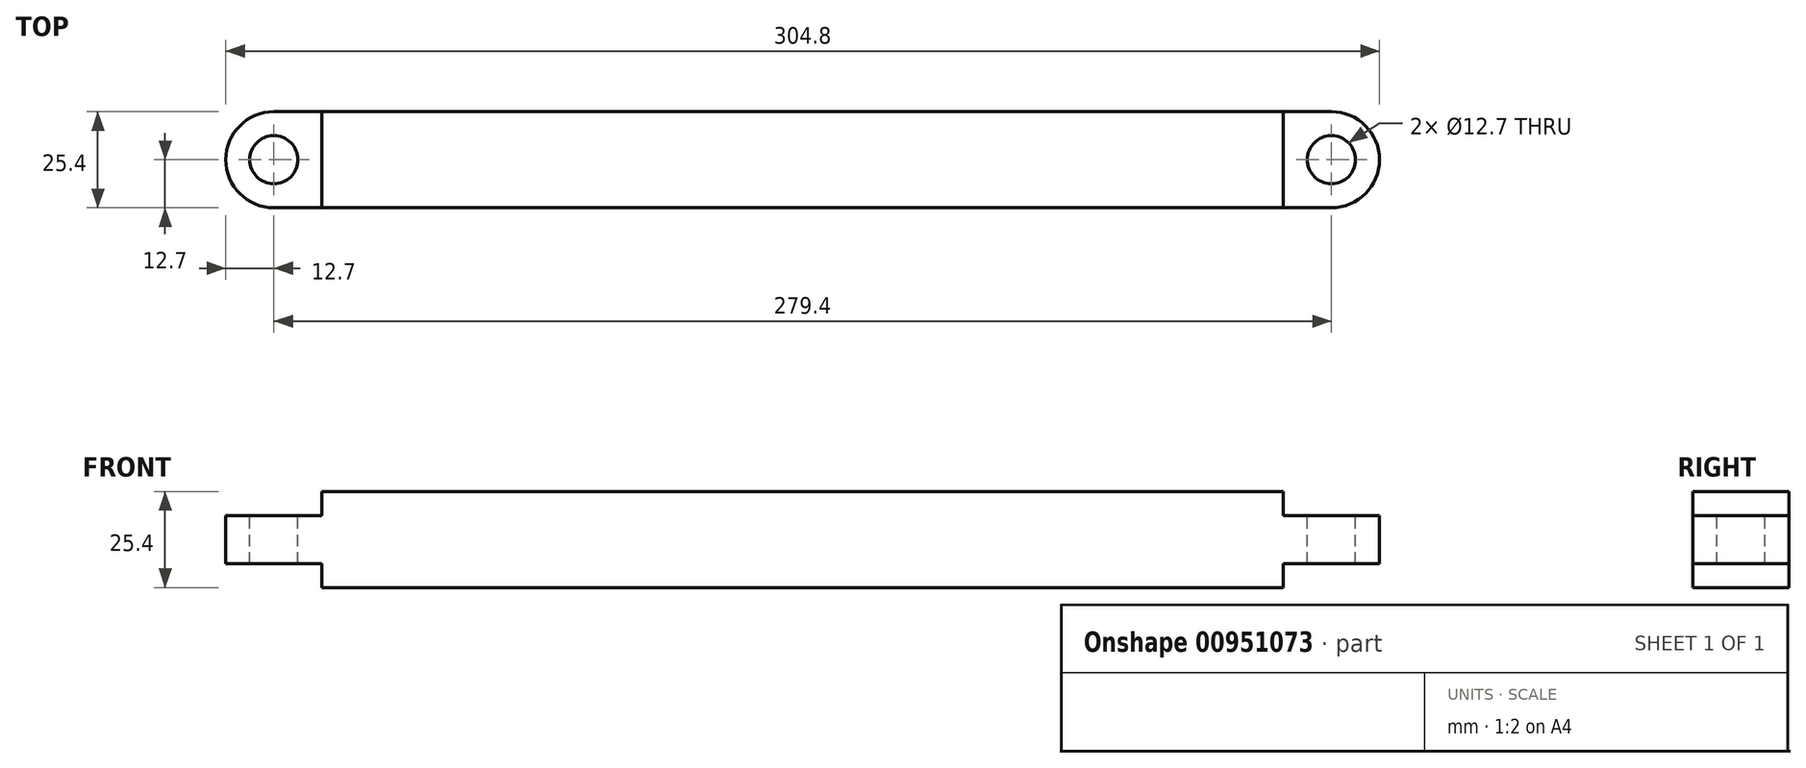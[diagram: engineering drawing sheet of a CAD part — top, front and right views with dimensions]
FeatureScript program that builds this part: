
annotation { "Feature Type Name" : "Feature", "Feature Type Description" : "" }
export const myFeature = defineFeature(function(context is Context, id is Id, definition is map)
    precondition{}
    {
        {
            var Q0;
            Q0=qCreatedBy(makeId("Top.planeOp"),FACE);
            var sketch = newSketch(context, id + "F0", { "sketchPlane" : qUnion([Q0])});
            skLineSegment(sketch, "E0.bottom", {"start": v(139.7, -12.7) * mm, "end": v(-139.7, -12.7) * mm});
            skLineSegment(sketch, "E0.top", {"start": v(139.7, 12.7) * mm, "end": v(-139.7, 12.7) * mm});
            skLineSegment(sketch, "E0.left", {"start": v(139.7, -12.7) * mm, "end": v(139.7, 12.7) * mm});
            skLineSegment(sketch, "E0.right", {"start": v(-139.7, -12.7) * mm, "end": v(-139.7, 12.7) * mm});
            skPoint(sketch, "E0.middle", {"position": v(0, 0) * mm});
            skArc(sketch, "E1", {"start": v(139.7, 12.7) * mm, "mid": v(152.4, 0) * mm, "end": v(139.7, -12.7) * mm});
            skArc(sketch, "E2", {"start": v(-139.7, 12.7) * mm, "mid": v(-152.4, 0) * mm, "end": v(-139.7, -12.7) * mm});
            skSolve(sketch);
        }
        {
            var Q0;
            Q0 = qSketchRegion(id + "F0", true);
            extrude(context, id + "F1", {"entities" : qUnion([Q0]), "depth" : 25.4 * mm, "offsetDistance" : 25.4 * mm});
        }
        {
            var Q0;
            Q0=makeQuery(id+"F1.opExtrude","CAP_FACE",FACE,{"disambiguationData":[OSD([sQuery(id+"F0.wireOp",EDGE,"E0.bottom"),sQuery(id+"F0.wireOp",EDGE,"E0.top"),sQuery(id+"F0.wireOp",EDGE,"E1"),sQuery(id+"F0.wireOp",EDGE,"E2")])],"isStart":false});
            var sketch = newSketch(context, id + "F2", { "sketchPlane" : qUnion([Q0])});
            skCircle(sketch, "E3", {"center": v(-139.7, 0) * mm, "radius": 6.35 * mm});
            skCircle(sketch, "E4", {"center": v(139.7, 0) * mm, "radius": 6.35 * mm});
            skSolve(sketch);
        }
        {
            var Q0;
            Q0 = qSketchRegion(id + "F2", true);
            var Q1;
            Q1=makeQuery(id+"F1.opExtrude","CAP_FACE",FACE,{"disambiguationData":[OSD([sQuery(id+"F0.wireOp",EDGE,"E0.bottom"),sQuery(id+"F0.wireOp",EDGE,"E0.top"),sQuery(id+"F0.wireOp",EDGE,"E1"),sQuery(id+"F0.wireOp",EDGE,"E2")])],"isStart":true});
            extrude(context, id + "F3", {"entities" : qUnion([Q0]), "operationType" : NewBodyOperationType.REMOVE, "endBound" : BoundingType.UP_TO_SURFACE, "oppositeDirection" : true, "depth" : 25.4 * mm, "endBoundEntityFace" : qUnion([Q1]), "offsetDistance" : 25.4 * mm});
        }
        {
            var Q0;
            Q0=makeQuery(id+"F1.opExtrude","SWEPT_FACE",FACE,{"disambiguationData":[OSD([sQuery(id+"F0.wireOp",EDGE,"E0.bottom")])]});
            var sketch = newSketch(context, id + "F4", { "sketchPlane" : qUnion([Q0])});
            skLineSegment(sketch, "E5.bottom", {"start": v(-96.3, 19.05) * mm, "end": v(-127, 19.05) * mm, "construction": true});
            skLineSegment(sketch, "E5.top", {"start": v(-96.3, 6.35) * mm, "end": v(-127, 6.35) * mm, "construction": true});
            skLineSegment(sketch, "E5.left", {"start": v(-127, 19.05) * mm, "end": v(-127, 6.35) * mm, "construction": true});
            skLineSegment(sketch, "E5.right", {"start": v(-96.3, 19.05) * mm, "end": v(-96.3, 6.35) * mm, "construction": true});
            skLineSegment(sketch, "E6", {"start": v(-127, 19.05) * mm, "end": v(-127, 25.4) * mm});
            skLineSegment(sketch, "E7", {"start": v(-127, 25.4) * mm, "end": v(-279.4, 25.4) * mm});
            skLineSegment(sketch, "E8", {"start": v(-279.4, 25.4) * mm, "end": v(-279.4, 19.05) * mm});
            skLineSegment(sketch, "E9", {"start": v(-279.4, 19.05) * mm, "end": v(-127, 19.05) * mm});
            skLineSegment(sketch, "E10", {"start": v(-127, 6.35) * mm, "end": v(-127, 0) * mm});
            skLineSegment(sketch, "E11", {"start": v(-127, 0) * mm, "end": v(-279.4, 0) * mm});
            skLineSegment(sketch, "E12", {"start": v(-279.4, 0) * mm, "end": v(-279.4, 6.35) * mm});
            skLineSegment(sketch, "E13", {"start": v(-279.4, 6.35) * mm, "end": v(-127, 6.35) * mm});
            skLineSegment(sketch, "E14", {"start": v(127, 25.4) * mm, "end": v(279.4, 25.4) * mm});
            skLineSegment(sketch, "E15", {"start": v(127, 19.05) * mm, "end": v(279.4, 19.05) * mm});
            skLineSegment(sketch, "E16", {"start": v(127, 6.35) * mm, "end": v(279.4, 6.35) * mm});
            skLineSegment(sketch, "E17", {"start": v(127, 0) * mm, "end": v(279.4, 0) * mm});
            skLineSegment(sketch, "E18", {"start": v(127, 25.4) * mm, "end": v(127, 19.05) * mm});
            skLineSegment(sketch, "E19", {"start": v(127, 6.35) * mm, "end": v(127, 0) * mm});
            skLineSegment(sketch, "E20", {"start": v(279.4, 25.4) * mm, "end": v(279.4, 19.05) * mm});
            skLineSegment(sketch, "E21", {"start": v(279.4, 6.35) * mm, "end": v(279.4, 0) * mm});
            skSolve(sketch);
        }
        {
            var Q0;
            Q0 = qSketchRegion(id + "F4", true);
            extrude(context, id + "F5", {"entities" : qUnion([Q0]), "operationType" : NewBodyOperationType.REMOVE, "endBound" : BoundingType.THROUGH_ALL, "oppositeDirection" : true, "depth" : 25.4 * mm, "offsetDistance" : 25.4 * mm});
        }
    });
